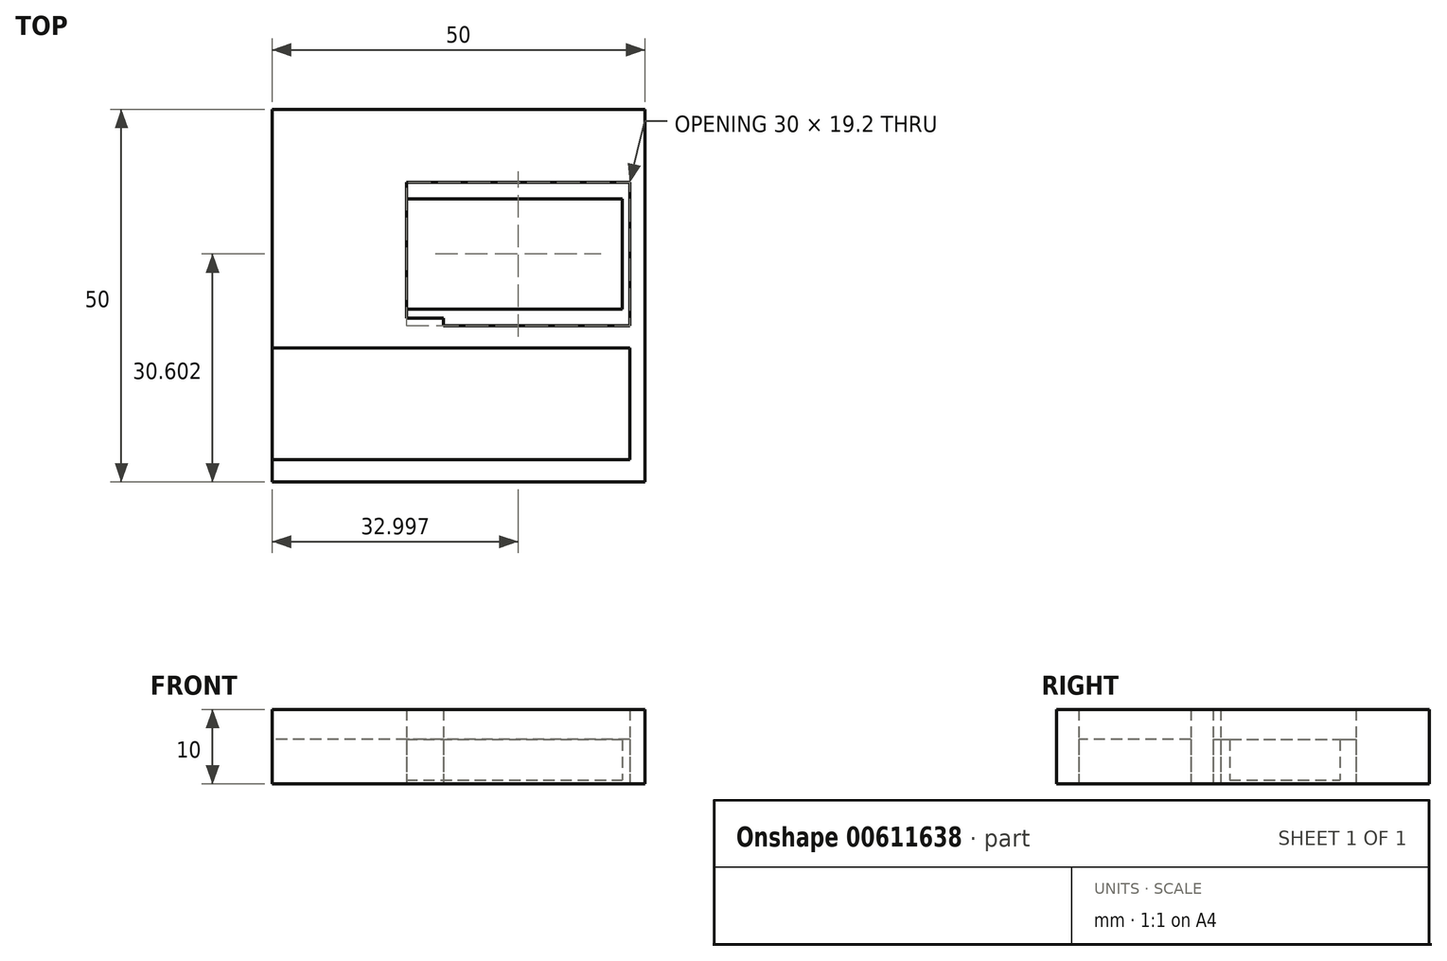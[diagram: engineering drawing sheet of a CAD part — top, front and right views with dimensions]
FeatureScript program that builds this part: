
annotation { "Feature Type Name" : "Feature", "Feature Type Description" : "" }
export const myFeature = defineFeature(function(context is Context, id is Id, definition is map)
    precondition{}
    {
        {
            var Q0;
            Q0=qCreatedBy(makeId("Top.planeOp"),FACE);
            var sketch = newSketch(context, id + "F0", { "sketchPlane" : qUnion([Q0])});
            skLineSegment(sketch, "E0.bottom", {"start": v(-26.5, 23.2) * mm, "end": v(23.5, 23.2) * mm});
            skLineSegment(sketch, "E0.top", {"start": v(-26.5, -26.8) * mm, "end": v(23.5, -26.8) * mm});
            skLineSegment(sketch, "E0.left", {"start": v(-26.5, 23.2) * mm, "end": v(-26.5, -26.8) * mm});
            skLineSegment(sketch, "E0.right", {"start": v(23.5, 23.2) * mm, "end": v(23.5, -26.8) * mm});
            skLineSegment(sketch, "E1", {"start": v(-1.5, -26.8) * mm, "end": v(-1.5, -23.8) * mm, "construction": true});
            skLineSegment(sketch, "E2", {"start": v(-26.5, -23.8) * mm, "end": v(23.5, -23.8) * mm});
            skLineSegment(sketch, "E3", {"start": v(23.5, -20.8) * mm, "end": v(21.5, -20.8) * mm, "construction": true});
            skLineSegment(sketch, "E4", {"start": v(21.5, -23.8) * mm, "end": v(21.5, -8.8) * mm});
            skLineSegment(sketch, "E5", {"start": v(21.5, -8.8) * mm, "end": v(-26.5, -8.8) * mm});
            skLineSegment(sketch, "E6", {"start": v(21.5, -8.8) * mm, "end": v(21.5, -5.8) * mm});
            skLineSegment(sketch, "E7", {"start": v(21.5, -5.8) * mm, "end": v(-3.5, -5.8) * mm});
            skLineSegment(sketch, "E8", {"start": v(-3.5, -5.8) * mm, "end": v(-3.5, -4.8) * mm});
            skLineSegment(sketch, "E9", {"start": v(-3.5, -4.8) * mm, "end": v(-8.5, -4.8) * mm});
            skLineSegment(sketch, "E10", {"start": v(-8.5, -4.8) * mm, "end": v(-8.5, 13.4) * mm});
            skLineSegment(sketch, "E11", {"start": v(-8.5, 13.4) * mm, "end": v(-3.5, 13.4) * mm});
            skLineSegment(sketch, "E12", {"start": v(-3.5, 13.4) * mm, "end": v(-3.5, 14.4) * mm});
            skLineSegment(sketch, "E13", {"start": v(9, -5.8) * mm, "end": v(9, -3.6) * mm, "construction": true});
            skPoint(sketch, "E13.endSnap0", {"position": v(9, -5.8) * mm});
            skLineSegment(sketch, "E14", {"start": v(21.5, 13.4) * mm, "end": v(-3.5, 13.4) * mm});
            skLineSegment(sketch, "E15", {"start": v(21.5, -5.8) * mm, "end": v(21.5, 13.4) * mm});
            skLineSegment(sketch, "E16", {"start": v(21.5, 3.8) * mm, "end": v(20.5, 3.8) * mm, "construction": true});
            skPoint(sketch, "E16.endSnap0", {"position": v(21.5, 3.8) * mm});
            skLineSegment(sketch, "E17", {"start": v(9, 13.4) * mm, "end": v(9, 11.2) * mm, "construction": true});
            skLineSegment(sketch, "E18", {"start": v(-8.5, -3.6) * mm, "end": v(20.5, -3.6) * mm});
            skLineSegment(sketch, "E19", {"start": v(20.5, -3.6) * mm, "end": v(20.5, 11.2) * mm});
            skLineSegment(sketch, "E20", {"start": v(20.5, 11.2) * mm, "end": v(-8.5, 11.2) * mm});
            skSolve(sketch);
        }
        {
            var Q0;
            {var subQ0=sQuery(id+"F0.wireOp",EDGE,"E18");Q0=makeQuery(id+"F0.imprint","IMPRINT",FACE,{"disambiguationData":[TD([[makeQuery(id+"F0.imprint","IMPRINT",EDGE,{"derivedFrom":subQ0}),1.0]])]});}
            extrude(context, id + "F1", {"entities" : qUnion([Q0]), "depth" : .5 * mm, "offsetDistance" : 25 * mm});
        }
        {
            var Q0;
            Q0=makeQuery(id+"F0.imprint","IMPRINT",FACE,{"disambiguationData":[TD([[makeQuery(id+"F0.imprint","IMPRINT",EDGE,{"derivedFrom":sQuery(id+"F0.wireOp",EDGE,"E7")}),-1.0]])]});
            extrude(context, id + "F2", {"entities" : qUnion([Q0]), "operationType" : NewBodyOperationType.ADD, "depth" : 5.95 * mm, "offsetDistance" : 25 * mm});
        }
        {
            var Q0;
            {var subQ4=sQuery(id+"F0.wireOp",EDGE,"E4");Q0=makeQuery(id+"F0.imprint","IMPRINT",FACE,{"disambiguationData":[TD([[makeQuery(id+"F0.imprint","IMPRINT",EDGE,{"derivedFrom":subQ4}),1.0]])]});}
            extrude(context, id + "F3", {"entities" : qUnion([Q0]), "depth" : 5.95 * mm, "offsetDistance" : 25 * mm});
        }
        {
            var Q0;
            {var subQ5=sQuery(id+"F0.wireOp",EDGE,"E0.bottom");Q0=makeQuery(id+"F0.imprint","IMPRINT",FACE,{"disambiguationData":[TD([[makeQuery(id+"F0.imprint","IMPRINT",EDGE,{"derivedFrom":subQ5}),-1.0]])]});}
            var Q1;
            {var subQ4=sQuery(id+"F0.wireOp",EDGE,"E0.top");Q1=makeQuery(id+"F0.imprint","IMPRINT",FACE,{"disambiguationData":[TD([[makeQuery(id+"F0.imprint","IMPRINT",EDGE,{"derivedFrom":subQ4}),1.0]])]});}
            extrude(context, id + "F4", {"entities" : qUnion([Q0, Q1]), "depth" : 10 * mm, "offsetDistance" : 25 * mm});
        }
    });
